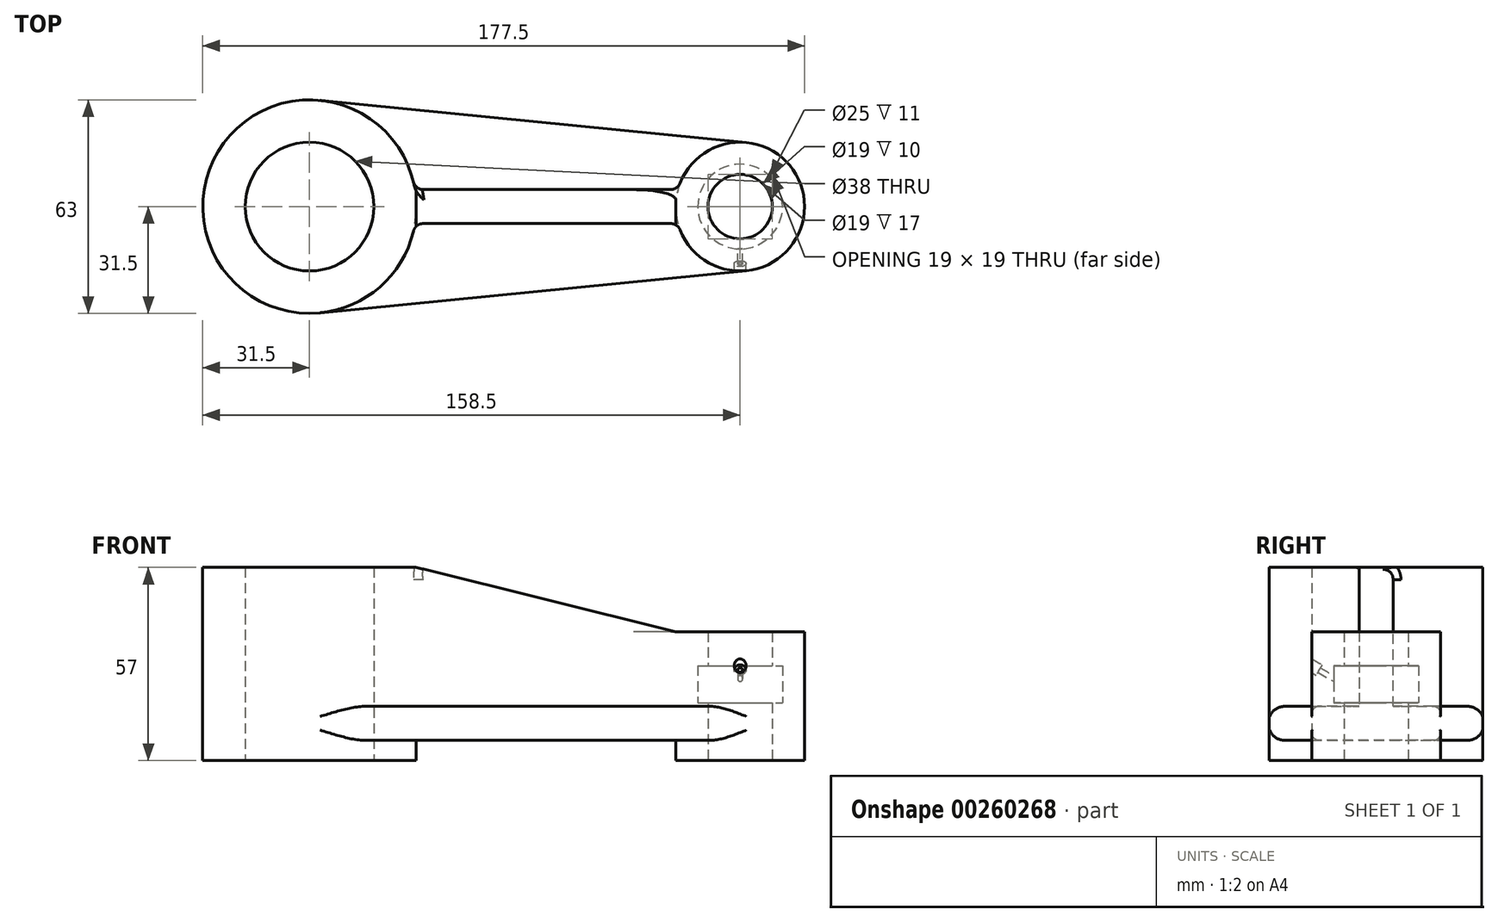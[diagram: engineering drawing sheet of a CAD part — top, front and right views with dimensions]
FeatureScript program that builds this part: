
annotation { "Feature Type Name" : "Feature", "Feature Type Description" : "" }
export const myFeature = defineFeature(function(context is Context, id is Id, definition is map)
    precondition{}
    {
        {
            var Q0;
            Q0=qCreatedBy(makeId("Top.planeOp"),FACE);
            var sketch = newSketch(context, id + "F0", { "sketchPlane" : qUnion([Q0])});
            skCircle(sketch, "E0", {"center": v(0, 0) * mm, "radius": 31.5 * mm});
            skCircle(sketch, "E1", {"center": v(0, 0) * mm, "radius": 19 * mm});
            skCircle(sketch, "E2", {"center": v(127, 0) * mm, "radius": 9.5 * mm});
            skCircle(sketch, "E3", {"center": v(127, 0) * mm, "radius": 19 * mm});
            skLineSegment(sketch, "E4", {"start": v(3.1, 31.35) * mm, "end": v(128.87, 18.9) * mm});
            skLineSegment(sketch, "E5", {"start": v(3.1, -31.35) * mm, "end": v(128.87, -18.9) * mm});
            skSolve(sketch);
        }
        {
            var Q0;
            {var subQ0=sQuery(id+"F0.wireOp",EDGE,"E4");Q0=makeQuery(id+"F0.imprint","IMPRINT",FACE,{"disambiguationData":[TD([[makeQuery(id+"F0.imprint","IMPRINT",EDGE,{"derivedFrom":subQ0}),-1.0]])]});}
            extrude(context, id + "F1", {"entities" : qUnion([Q0]), "depth" : 10 * mm});
        }
        {
            var Q0;
            Q0=makeQuery(id+"F0.imprint","IMPRINT",FACE,{"disambiguationData":[TD([[makeQuery(id+"F0.imprint","IMPRINT",EDGE,{"derivedFrom":sQuery(id+"F0.wireOp",EDGE,"E1")}),-1.0]])]});
            extrude(context, id + "F2", {"entities" : qUnion([Q0]), "operationType" : NewBodyOperationType.ADD, "depth" : (57 - 6) * mm});
        }
        {
            var Q0;
            Q0=makeQuery(id+"F0.imprint","IMPRINT",FACE,{"disambiguationData":[TD([[makeQuery(id+"F0.imprint","IMPRINT",EDGE,{"derivedFrom":sQuery(id+"F0.wireOp",EDGE,"E2")}),-1.0]])]});
            extrude(context, id + "F3", {"entities" : qUnion([Q0]), "operationType" : NewBodyOperationType.ADD, "depth" : (38 - 6) * mm});
        }
        {
            var Q0;
            Q0=makeQuery(id+"F0.imprint","IMPRINT",FACE,{"disambiguationData":[TD([[makeQuery(id+"F0.imprint","IMPRINT",EDGE,{"derivedFrom":sQuery(id+"F0.wireOp",EDGE,"E1")}),-1.0]])]});
            var Q1;
            Q1=makeQuery(id+"F0.imprint","IMPRINT",FACE,{"disambiguationData":[TD([[makeQuery(id+"F0.imprint","IMPRINT",EDGE,{"derivedFrom":sQuery(id+"F0.wireOp",EDGE,"E2")}),-1.0]])]});
            extrude(context, id + "F4", {"entities" : qUnion([Q0, Q1]), "operationType" : NewBodyOperationType.ADD, "oppositeDirection" : true, "depth" : 6 * mm});
        }
        {
            var Q0;
            Q0=qCreatedBy(makeId("Front.planeOp"),FACE);
            var sketch = newSketch(context, id + "F5", { "sketchPlane" : qUnion([Q0])});
            skLineSegment(sketch, "E6", {"start": v(31.5, 51) * mm, "end": v(31.5, 10) * mm});
            skLineSegment(sketch, "E7", {"start": v(31.5, 0) * mm, "end": v(31.5, -6) * mm});
            skLineSegment(sketch, "E8", {"start": v(-31.5, -6) * mm, "end": v(-31.5, 51) * mm});
            skLineSegment(sketch, "E9", {"start": v(108, 10) * mm, "end": v(108, 32) * mm});
            skLineSegment(sketch, "E10", {"start": v(146, 32) * mm, "end": v(146, -6) * mm});
            skLineSegment(sketch, "E11", {"start": v(108, -6) * mm, "end": v(108, 0) * mm});
            skLineSegment(sketch, "E12", {"start": v(19, 51) * mm, "end": v(19, -6) * mm});
            skLineSegment(sketch, "E13", {"start": v(-19, -6) * mm, "end": v(-19, 51) * mm});
            skLineSegment(sketch, "E14", {"start": v(136.5, 32) * mm, "end": v(136.5, -6) * mm});
            skLineSegment(sketch, "E15", {"start": v(117.5, -6) * mm, "end": v(117.5, 32) * mm});
            skLineSegment(sketch, "E16", {"start": v(108, 10) * mm, "end": v(31.5, 10) * mm});
            skLineSegment(sketch, "E17", {"start": v(31.5, 51) * mm, "end": v(108, 32) * mm});
            skLineSegment(sketch, "E18", {"start": v(113.09, 32) * mm, "end": v(113.09, 10) * mm});
            skLineSegment(sketch, "E19", {"start": v(113.09, 10) * mm, "end": v(108, 10) * mm});
            skLineSegment(sketch, "E20", {"start": v(113.09, 32) * mm, "end": v(108, 32) * mm});
            skLineSegment(sketch, "E21", {"start": v(31.5, 51) * mm, "end": v(25.58, 51) * mm});
            skLineSegment(sketch, "E22", {"start": v(25.58, 51) * mm, "end": v(25.58, 10) * mm});
            skLineSegment(sketch, "E23", {"start": v(25.58, 10) * mm, "end": v(31.5, 10) * mm});
            skLineSegment(sketch, "E24", {"start": v(127, 39.76) * mm, "end": v(127, -14.63) * mm, "construction": true});
            skLineSegment(sketch, "E25.bottom", {"start": v(136.5, 22) * mm, "end": v(139.5, 22) * mm});
            skLineSegment(sketch, "E25.top", {"start": v(136.5, 11) * mm, "end": v(139.5, 11) * mm});
            skLineSegment(sketch, "E25.left", {"start": v(136.5, 22) * mm, "end": v(136.5, 11) * mm});
            skLineSegment(sketch, "E25.right", {"start": v(139.5, 22) * mm, "end": v(139.5, 11) * mm});
            skSolve(sketch);
        }
        {
            var Q0;
            Q0=makeQuery(id+"F5.imprint","IMPRINT",FACE,{"disambiguationData":[TD([[makeQuery(id+"F5.imprint","IMPRINT",EDGE,{"derivedFrom":sQuery(id+"F5.wireOp",EDGE,"E6")}),-1.0]])]});
            var Q1;
            Q1=makeQuery(id+"F5.imprint","IMPRINT",FACE,{"disambiguationData":[TD([[makeQuery(id+"F5.imprint","IMPRINT",EDGE,{"derivedFrom":sQuery(id+"F5.wireOp",EDGE,"E6")}),1.0]])]});
            var Q2;
            Q2=makeQuery(id+"F5.imprint","IMPRINT",FACE,{"disambiguationData":[TD([[makeQuery(id+"F5.imprint","IMPRINT",EDGE,{"derivedFrom":sQuery(id+"F5.wireOp",EDGE,"E9")}),-1.0]])]});
            extrude(context, id + "F6", {"entities" : qUnion([Q0, Q1, Q2]), "operationType" : NewBodyOperationType.ADD, "depth" : 10 * mm, "symmetric" : true});
        }
        {
            var Q0;
            Q0=makeQuery(id+"F5.imprint","IMPRINT",FACE,{"disambiguationData":[TD([[makeQuery(id+"F5.imprint","IMPRINT",EDGE,{"derivedFrom":sQuery(id+"F5.wireOp",EDGE,"E25.bottom")}),-1.0]])]});
            var Q1;
            Q1=sQuery(id+"F5.wireOp",EDGE,"E24");
            revolve(context, id + "F7", {"operationType" : NewBodyOperationType.REMOVE, "entities" : qUnion([Q0]), "axis" : qUnion([Q1]), "revolveType" : RevolveType.FULL, "oppositeDirection" : true});
        }
        {
            var Q0;
            Q0=qCreatedBy(makeId("Right.planeOp"),FACE);
            var Q1;
            Q1=sQuery(id+"F5.wireOp",VERTEX,"E24.start");
            cPlane(context, id + "F8", {"entities" : qUnion([Q0, Q1]), "cplaneType" : CPlaneType.PLANE_POINT, "offset" : 25 * mm, "width" : 150 * mm, "height" : 150 * mm});
        }
        {
            var Q0;
            Q0=qCreatedBy(id+"F8.planeOp",FACE);
            var sketch = newSketch(context, id + "F9", { "sketchPlane" : qUnion([Q0])});
            skLineSegment(sketch, "E26", {"start": v(-19, 10) * mm, "end": v(-19, 32) * mm, "construction": true});
            skLineSegment(sketch, "E27", {"start": v(19, 32) * mm, "end": v(19, 10) * mm});
            skLineSegment(sketch, "E28", {"start": v(19, 0) * mm, "end": v(19, -6) * mm});
            skLineSegment(sketch, "E29", {"start": v(-19, -6) * mm, "end": v(-19, 0) * mm});
            skLineSegment(sketch, "E30", {"start": v(9.5, 32) * mm, "end": v(9.5, 22) * mm});
            skLineSegment(sketch, "E31", {"start": v(-9.5, 22) * mm, "end": v(-9.5, 32) * mm, "construction": true});
            skLineSegment(sketch, "E32", {"start": v(-9.5, 22) * mm, "end": v(-9.5, 9.14) * mm, "construction": true});
            skLineSegment(sketch, "E33", {"start": v(-23.68, 24.72) * mm, "end": v(-6.55, 14.77) * mm, "construction": true});
            skLineSegment(sketch, "E34", {"start": v(-21.62, 23.52) * mm, "end": v(-20.74, 25.03) * mm});
            skLineSegment(sketch, "E35", {"start": v(-20.74, 25.03) * mm, "end": v(-15.96, 22.26) * mm});
            skLineSegment(sketch, "E36", {"start": v(-15.96, 22.26) * mm, "end": v(-16.46, 21.4) * mm});
            skLineSegment(sketch, "E37", {"start": v(-16.46, 21.4) * mm, "end": v(-6.25, 15.46) * mm});
            skLineSegment(sketch, "E38", {"start": v(-6.25, 15.46) * mm, "end": v(-6.63, 14.81) * mm});
            skLineSegment(sketch, "E39", {"start": v(-6.63, 14.81) * mm, "end": v(-21.62, 23.52) * mm});
            skPoint(sketch, "E40", {"position": v(-19, 22) * mm});
            skSolve(sketch);
        }
        {
            var Q0;
            Q0=makeQuery(id+"F9.imprint","IMPRINT",FACE,{"disambiguationData":[TD([[makeQuery(id+"F9.imprint","IMPRINT",EDGE,{"derivedFrom":sQuery(id+"F9.wireOp",EDGE,"E34")}),-1.0]])]});
            var Q1;
            Q1=sQuery(id+"F9.wireOp",EDGE,"E33");
            revolve(context, id + "F10", {"operationType" : NewBodyOperationType.REMOVE, "entities" : qUnion([Q0]), "axis" : qUnion([Q1]), "revolveType" : RevolveType.FULL, "oppositeDirection" : true});
        }
        {
            var Q0;
            Q0=makeQuery(id+"F6.opExtrude","CAP_EDGE",EDGE,{"disambiguationData":[OSD([sQuery(id+"F5.wireOp",EDGE,"E17")])],"isStart":true});
            var Q1;
            Q1=makeQuery(id+"F6.opExtrude","CAP_EDGE",EDGE,{"disambiguationData":[OSD([sQuery(id+"F5.wireOp",EDGE,"E16"),sQuery(id+"F5.wireOp",EDGE,"E19"),sQuery(id+"F5.wireOp",EDGE,"E23")])],"isStart":true});
            var Q2;
            {var subQ0=sQuery(id+"F0.wireOp",EDGE,"E0");var subQ1=sQuery(id+"F0.wireOp",EDGE,"E4");Q2=makeQuery(id+"F6.boolean.opBoolean","SPLIT",EDGE,{"disambiguationData":[TD([makeQuery(id+"F1.opExtrude","SWEPT_FACE",FACE,{"disambiguationData":[OSD([subQ1])]})])],"derivedFrom":makeQuery(id+"F1.opExtrude","CAP_EDGE",EDGE,{"disambiguationData":[OSD([subQ0])],"isStart":false})});}
            var Q3;
            Q3=makeQuery(id+"F1.opExtrude","CAP_EDGE",EDGE,{"disambiguationData":[OSD([sQuery(id+"F0.wireOp",EDGE,"E4")])],"isStart":false});
            var Q4;
            Q4=makeQuery(id+"F1.opExtrude","CAP_EDGE",EDGE,{"disambiguationData":[OSD([sQuery(id+"F0.wireOp",EDGE,"E4")])],"isStart":true});
            var Q5;
            Q5=makeQuery(id+"F1.opExtrude","CAP_EDGE",EDGE,{"disambiguationData":[OSD([sQuery(id+"F0.wireOp",EDGE,"E5")])],"isStart":true});
            var Q6;
            Q6=makeQuery(id+"F1.opExtrude","CAP_EDGE",EDGE,{"disambiguationData":[OSD([sQuery(id+"F0.wireOp",EDGE,"E5")])],"isStart":false});
            var Q7;
            {var subQ0=sQuery(id+"F0.wireOp",EDGE,"E0");var subQ1=sQuery(id+"F0.wireOp",EDGE,"E5");Q7=makeQuery(id+"F6.boolean.opBoolean","SPLIT",EDGE,{"disambiguationData":[TD([makeQuery(id+"F1.opExtrude","SWEPT_FACE",FACE,{"disambiguationData":[OSD([subQ1])]})])],"derivedFrom":makeQuery(id+"F1.opExtrude","CAP_EDGE",EDGE,{"disambiguationData":[OSD([subQ0])],"isStart":false})});}
            var Q8;
            Q8=makeQuery(id+"F6.opExtrude","CAP_EDGE",EDGE,{"disambiguationData":[OSD([sQuery(id+"F5.wireOp",EDGE,"E16"),sQuery(id+"F5.wireOp",EDGE,"E19"),sQuery(id+"F5.wireOp",EDGE,"E23")])],"isStart":false});
            var Q9;
            {var subQ0=sQuery(id+"F0.wireOp",EDGE,"E0");Q9=makeQuery(id+"F6.boolean.opBoolean","INTERSECT",EDGE,{"derivedFrom":[makeQuery(id+"F4.boolean.opBoolean","MERGE",FACE,{"derivedFrom":[makeQuery(id+"F2.opExtrude","SWEPT_FACE",FACE,{"disambiguationData":[OSD([subQ0])]}),makeQuery(id+"F4.opExtrude","SWEPT_FACE",FACE,{"disambiguationData":[OSD([subQ0])]})]}),makeQuery(id+"F6.opExtrude","CAP_FACE",FACE,{"disambiguationData":[OSD([sQuery(id+"F5.wireOp",EDGE,"E16"),sQuery(id+"F5.wireOp",EDGE,"E17"),sQuery(id+"F5.wireOp",EDGE,"E18"),sQuery(id+"F5.wireOp",EDGE,"E19"),sQuery(id+"F5.wireOp",EDGE,"E20"),sQuery(id+"F5.wireOp",EDGE,"E21"),sQuery(id+"F5.wireOp",EDGE,"E22"),sQuery(id+"F5.wireOp",EDGE,"E23")])],"isStart":false})]});}
            var Q10;
            Q10=makeQuery(id+"F4.opExtrude","CAP_EDGE",EDGE,{"disambiguationData":[OSD([sQuery(id+"F0.wireOp",EDGE,"E0")])],"isStart":true});
            var Q11;
            Q11=makeQuery(id+"F4.opExtrude","CAP_EDGE",EDGE,{"disambiguationData":[OSD([sQuery(id+"F0.wireOp",EDGE,"E3")])],"isStart":true});
            fillet(context, id + "F11", {"entities" : qUnion([Q0, Q1, Q2, Q3, Q4, Q5, Q6, Q7, Q8, Q9, Q10, Q11]), "radius" : 3 * mm, "tangentPropagation" : true, "allowEdgeOverflow" : false});
        }
        {
            var Q0;
            {var subQ0=sQuery(id+"F0.wireOp",EDGE,"E3");Q0=makeQuery(id+"F6.boolean.opBoolean","INTERSECT",EDGE,{"derivedFrom":[makeQuery(id+"F4.boolean.opBoolean","MERGE",FACE,{"derivedFrom":[makeQuery(id+"F3.opExtrude","SWEPT_FACE",FACE,{"disambiguationData":[OSD([subQ0])]}),makeQuery(id+"F4.opExtrude","SWEPT_FACE",FACE,{"disambiguationData":[OSD([subQ0])]})]}),makeQuery(id+"F6.opExtrude","CAP_FACE",FACE,{"disambiguationData":[OSD([sQuery(id+"F5.wireOp",EDGE,"E16"),sQuery(id+"F5.wireOp",EDGE,"E17"),sQuery(id+"F5.wireOp",EDGE,"E18"),sQuery(id+"F5.wireOp",EDGE,"E19"),sQuery(id+"F5.wireOp",EDGE,"E20"),sQuery(id+"F5.wireOp",EDGE,"E21"),sQuery(id+"F5.wireOp",EDGE,"E22"),sQuery(id+"F5.wireOp",EDGE,"E23")])],"isStart":true})]});}
            var Q1;
            {var subQ0=sQuery(id+"F0.wireOp",EDGE,"E0");Q1=makeQuery(id+"F6.boolean.opBoolean","INTERSECT",EDGE,{"derivedFrom":[makeQuery(id+"F4.boolean.opBoolean","MERGE",FACE,{"derivedFrom":[makeQuery(id+"F2.opExtrude","SWEPT_FACE",FACE,{"disambiguationData":[OSD([subQ0])]}),makeQuery(id+"F4.opExtrude","SWEPT_FACE",FACE,{"disambiguationData":[OSD([subQ0])]})]}),makeQuery(id+"F6.opExtrude","CAP_FACE",FACE,{"disambiguationData":[OSD([sQuery(id+"F5.wireOp",EDGE,"E16"),sQuery(id+"F5.wireOp",EDGE,"E17"),sQuery(id+"F5.wireOp",EDGE,"E18"),sQuery(id+"F5.wireOp",EDGE,"E19"),sQuery(id+"F5.wireOp",EDGE,"E20"),sQuery(id+"F5.wireOp",EDGE,"E21"),sQuery(id+"F5.wireOp",EDGE,"E22"),sQuery(id+"F5.wireOp",EDGE,"E23")])],"isStart":true})]});}
            var Q2;
            {var subQ0=sQuery(id+"F0.wireOp",EDGE,"E3");Q2=makeQuery(id+"F6.boolean.opBoolean","INTERSECT",EDGE,{"derivedFrom":[makeQuery(id+"F4.boolean.opBoolean","MERGE",FACE,{"derivedFrom":[makeQuery(id+"F3.opExtrude","SWEPT_FACE",FACE,{"disambiguationData":[OSD([subQ0])]}),makeQuery(id+"F4.opExtrude","SWEPT_FACE",FACE,{"disambiguationData":[OSD([subQ0])]})]}),makeQuery(id+"F6.opExtrude","CAP_FACE",FACE,{"disambiguationData":[OSD([sQuery(id+"F5.wireOp",EDGE,"E16"),sQuery(id+"F5.wireOp",EDGE,"E17"),sQuery(id+"F5.wireOp",EDGE,"E18"),sQuery(id+"F5.wireOp",EDGE,"E19"),sQuery(id+"F5.wireOp",EDGE,"E20"),sQuery(id+"F5.wireOp",EDGE,"E21"),sQuery(id+"F5.wireOp",EDGE,"E22"),sQuery(id+"F5.wireOp",EDGE,"E23")])],"isStart":false})]});}
            fillet(context, id + "F12", {"entities" : qUnion([Q0, Q1, Q2]), "radius" : 3 * mm, "tangentPropagation" : true, "allowEdgeOverflow" : false});
        }
    });
